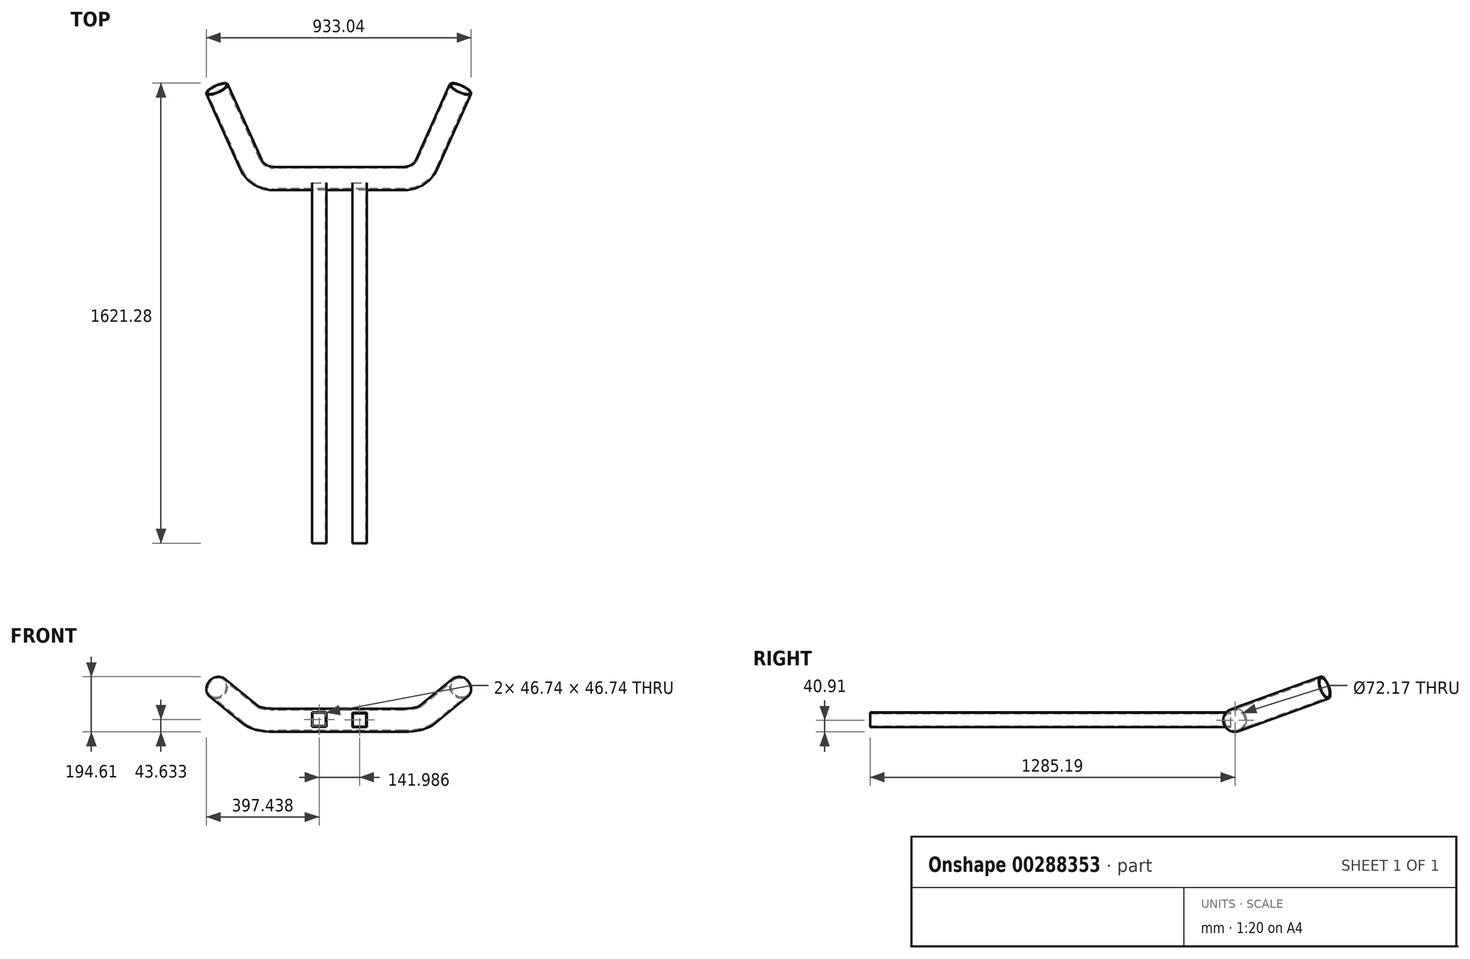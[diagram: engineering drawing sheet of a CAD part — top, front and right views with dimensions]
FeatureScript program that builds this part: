
annotation { "Feature Type Name" : "Feature", "Feature Type Description" : "" }
export const myFeature = defineFeature(function(context is Context, id is Id, definition is map)
    precondition{}
    {
        {
            var Q0;
            Q0=qCreatedBy(makeId("Front.planeOp"),FACE);
            var sketch = newSketch(context, id + "F0", { "sketchPlane" : qUnion([Q0])});
            skLineSegment(sketch, "E0.bottom", {"start": v(-94.48, -22.68) * mm, "end": v(-43.68, -22.68) * mm});
            skLineSegment(sketch, "E0.top", {"start": v(-94.48, 28.12) * mm, "end": v(-43.68, 28.12) * mm});
            skLineSegment(sketch, "E0.left", {"start": v(-94.48, -22.68) * mm, "end": v(-94.48, 28.12) * mm});
            skLineSegment(sketch, "E0.right", {"start": v(-43.68, -22.68) * mm, "end": v(-43.68, 28.12) * mm});
            skLineSegment(sketch, "E1.0", {"start": v(-92.45, -20.65) * mm, "end": v(-92.45, 26.1) * mm});
            skLineSegment(sketch, "E1.1", {"start": v(-92.45, -20.65) * mm, "end": v(-45.71, -20.65) * mm});
            skLineSegment(sketch, "E1.2", {"start": v(-45.71, -20.65) * mm, "end": v(-45.71, 26.1) * mm});
            skLineSegment(sketch, "E1.3", {"start": v(-92.45, 26.1) * mm, "end": v(-45.71, 26.1) * mm});
            skLineSegment(sketch, "E2.bottom", {"start": v(47.5, -24.85) * mm, "end": v(98.3, -24.85) * mm});
            skLineSegment(sketch, "E2.top", {"start": v(47.5, 25.95) * mm, "end": v(98.3, 25.95) * mm});
            skLineSegment(sketch, "E2.left", {"start": v(47.5, -24.85) * mm, "end": v(47.5, 25.95) * mm});
            skLineSegment(sketch, "E2.right", {"start": v(98.3, -24.85) * mm, "end": v(98.3, 25.95) * mm});
            skLineSegment(sketch, "E3.0", {"start": v(49.54, -22.82) * mm, "end": v(49.54, 23.91) * mm});
            skLineSegment(sketch, "E3.1", {"start": v(49.54, -22.82) * mm, "end": v(96.27, -22.82) * mm});
            skLineSegment(sketch, "E3.2", {"start": v(96.27, -22.82) * mm, "end": v(96.27, 23.91) * mm});
            skLineSegment(sketch, "E3.3", {"start": v(49.54, 23.91) * mm, "end": v(96.27, 23.91) * mm});
            skSolve(sketch);
        }
        {
            var Q0;
            Q0=qCreatedBy(makeId("Top.planeOp"),FACE);
            var sketch = newSketch(context, id + "F1", { "sketchPlane" : qUnion([Q0])});
            skLineSegment(sketch, "E4", {"start": v(0, 0) * mm, "end": v(168.92, 0) * mm});
            skSolve(sketch);
        }
        {
            var Q0;
            Q0 = qBodyType(qCreatedBy(id + "F1" ,EDGE), BodyType.WIRE);
            var Q1;
            Q1=qCreatedBy(makeId("Top.planeOp"),FACE);
            cPlane(context, id + "F2", {"entities" : qUnion([Q0, Q1]), "cplaneType" : CPlaneType.LINE_ANGLE, "offset" : 25.4 * mm, "angle" : 160 * degree, "oppositeDirection" : true, "width" : 152.4 * mm, "height" : 152.4 * mm});
        }
        {
            var Q0;
            Q0=makeQuery(id+"F0.imprint","IMPRINT",FACE,{"disambiguationData":[TD([[makeQuery(id+"F0.imprint","IMPRINT",EDGE,{"derivedFrom":sQuery(id+"F0.wireOp",EDGE,"E0.bottom")}),1.0]])]});
            extrude(context, id + "F3", {"entities" : qUnion([Q0]), "depth" : 1270 * mm});
        }
        {
            var Q0;
            Q0=makeQuery(id+"F0.imprint","IMPRINT",FACE,{"disambiguationData":[TD([[makeQuery(id+"F0.imprint","IMPRINT",EDGE,{"derivedFrom":sQuery(id+"F0.wireOp",EDGE,"E2.bottom")}),1.0]])]});
            extrude(context, id + "F4", {"entities" : qUnion([Q0]), "depth" : 1270 * mm});
        }
        {
            var Q0;
            Q0=qCreatedBy(id+"F2.planeOp",FACE);
            var sketch = newSketch(context, id + "F5", { "sketchPlane" : qUnion([Q0])});
            skLineSegment(sketch, "E5", {"start": v(-441.97, 344.62) * mm, "end": v(-322.99, 62.16) * mm});
            skLineSegment(sketch, "E6", {"start": v(-229.36, 0) * mm, "end": v(229.36, 0) * mm});
            skLineSegment(sketch, "E7", {"start": v(322.99, 62.16) * mm, "end": v(441.97, 344.62) * mm});
            skPoint(sketch, "E8.visualSharp", {"position": v(-296.8, 0) * mm});
            skArc(sketch, "E8.filletArc", {"start": v(-322.99, 62.16) * mm, "mid": v(-285.55, 16.95) * mm, "end": v(-229.36, 0) * mm});
            skPoint(sketch, "E9.visualSharp", {"position": v(296.8, 0) * mm});
            skArc(sketch, "E9.filletArc", {"start": v(229.36, 0) * mm, "mid": v(285.55, 16.95) * mm, "end": v(322.99, 62.16) * mm});
            skSolve(sketch);
        }
        {
            var Q0;
            Q0=qCreatedBy(makeId("Right.planeOp"),FACE);
            var Q1;
            Q1=sQuery(id+"F5.wireOp",VERTEX,"E9.filletArc.start");
            cPlane(context, id + "F6", {"entities" : qUnion([Q0, Q1]), "cplaneType" : CPlaneType.PLANE_POINT, "offset" : 231.2 * mm, "width" : 152.4 * mm, "height" : 152.4 * mm});
        }
        {
            var Q0;
            Q0=qCreatedBy(id+"F6.planeOp",FACE);
            var sketch = newSketch(context, id + "F7", { "sketchPlane" : qUnion([Q0])});
            skCircle(sketch, "E10", {"center": v(15.19, 0) * mm, "radius": 40.9 * mm});
            skCircle(sketch, "E11.0", {"center": v(15.19, 0) * mm, "radius": 36.08 * mm});
            skSolve(sketch);
        }
        {
            var Q0;
            Q0=makeQuery(id+"F7.imprint","IMPRINT",FACE,{"disambiguationData":[TD([[makeQuery(id+"F7.imprint","IMPRINT",EDGE,{"derivedFrom":sQuery(id+"F7.wireOp",EDGE,"E10")}),1.0]])]});
            var Q1;
            Q1=sQuery(id+"F5.wireOp",EDGE,"E6");
            var Q2;
            Q2=sQuery(id+"F5.wireOp",EDGE,"E8.filletArc");
            var Q3;
            Q3=sQuery(id+"F5.wireOp",EDGE,"E5");
            sweep(context, id + "F8", {"profiles" : qUnion([Q0]), "path" : qUnion([Q1, Q2, Q3])});
        }
        {
            var Q0;
            Q0 = qSketchRegion(id + "F5", true);
            var Q1;
            Q1=makeQuery(id+"F8.opSweep","CAP_FACE",FACE,{"disambiguationData":[OSD([sQuery(id+"F5.wireOp",VERTEX,"E6.end"),sQuery(id+"F7.wireOp",EDGE,"E10"),sQuery(id+"F7.wireOp",EDGE,"E11.0")])],"isStart":true});
            var Q2;
            Q2=sQuery(id+"F5.wireOp",EDGE,"E9.filletArc");
            var Q3;
            Q3=sQuery(id+"F5.wireOp",EDGE,"E7");
            sweep(context, id + "F9", {"operationType" : NewBodyOperationType.ADD, "profiles" : qUnion([Q0, Q1]), "path" : qUnion([Q2, Q3])});
        }
    });
